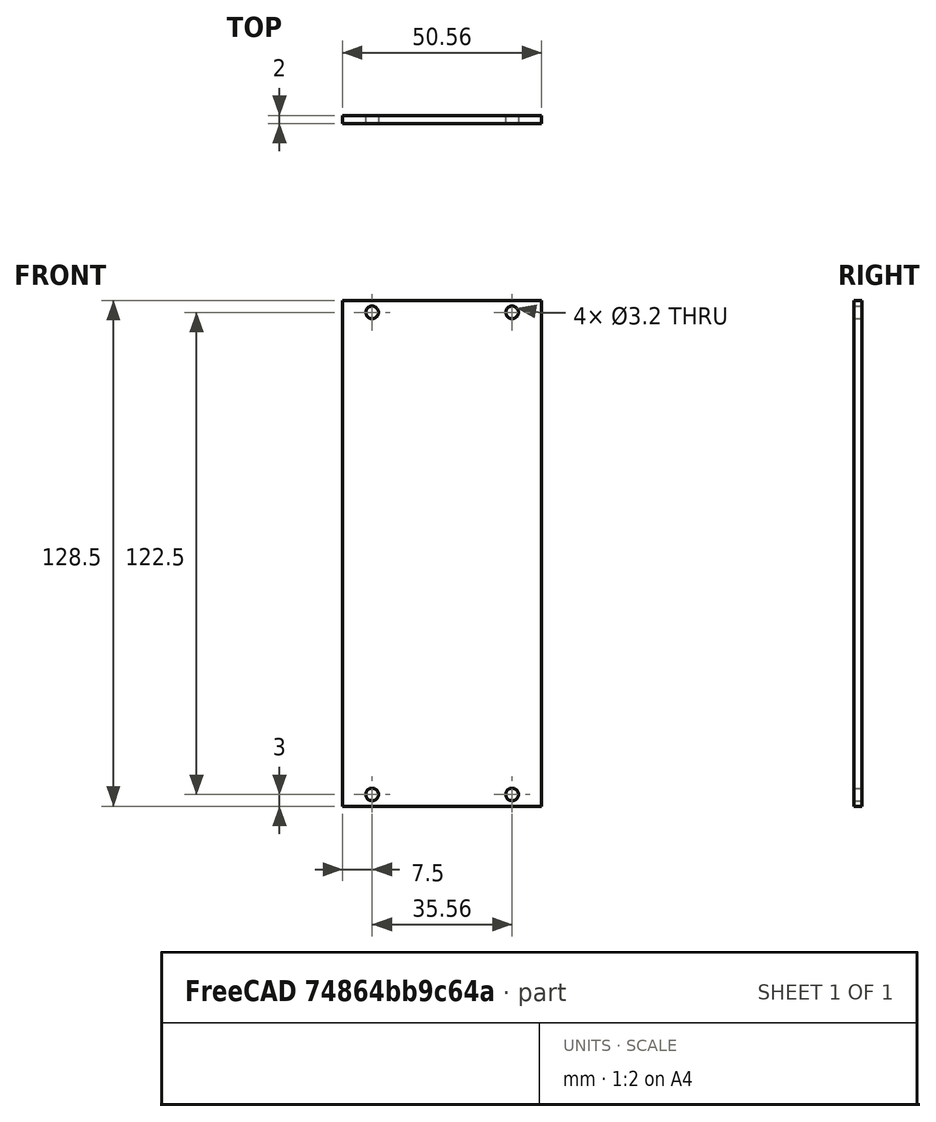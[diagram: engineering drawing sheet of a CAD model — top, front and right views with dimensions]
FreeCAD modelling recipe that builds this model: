
FCSTD DOCUMENT  (FreeCAD 1.0R38641 +468 (Git))
Label: 10hp_plate
License: All rights reserved
LicenseURL: https://en.wikipedia.org/wiki/All_rights_reserved
objects: Sketcher::SketchObject×1, PartDesign::Pad×1, PartDesign::Body×1, App::VarSet×1
note: 6 computed .brp shape members not serialized (recipe doc carries the construction recipe); baked Part::Feature solids carry a one-line shape summary decoded from their .brp
EXTERNAL_REF file=plate_dims.FCStd obj=VarSet

FEATURE [Sketcher::SketchObject] Sketch
  ArcFitTolerance = 1e-06
  AttachmentSupport = -> [XZ_Plane]
  FullyConstrained = true
  MakeInternals = false
  MapMode = 5
  Placement = pos=(0,0,0) rot=(1,0,0;1.5708rad)
  expr: Constraints[39] = <<plate_dims>>#VarSet.HoleOffsetY
  expr: Constraints[40] = <<plate_dims>>#VarSet.HoleOffsetX
  expr: Constraints[48] = <<plate_dims>>#VarSet.HoleDiameter
  expr: Constraints[49] = <<plate_dims>>#VarSet.PlateHeight
  expr: Constraints[52] = <<plate_dims>>#VarSet.HoleSpacing * (VarSet.PlateWidthHP - 3)
  sketch-geometry (20):
    g0: LineSegment StartX=-25.28 StartY=64.25 StartZ=0 EndX=-25.28 EndY=-64.25 EndZ=0
    g1: LineSegment StartX=-25.28 StartY=-64.25 StartZ=0 EndX=25.28 EndY=-64.25 EndZ=0
    g2: LineSegment StartX=25.28 StartY=-64.25 StartZ=0 EndX=25.28 EndY=64.25 EndZ=0
    g3: LineSegment StartX=25.28 StartY=64.25 StartZ=0 EndX=-25.28 EndY=64.25 EndZ=0
    g4: LineSegment [constr] StartX=17.78 StartY=61.25 StartZ=0 EndX=25.28 EndY=61.25 EndZ=0
    g5: LineSegment [constr] StartX=17.78 StartY=64.25 StartZ=0 EndX=17.78 EndY=61.25 EndZ=0
    g6: LineSegment [constr] StartX=17.78 StartY=61.25 StartZ=0 EndX=17.78 EndY=-61.25 EndZ=0
    g7: LineSegment [constr] StartX=17.78 StartY=-61.25 StartZ=0 EndX=17.78 EndY=-64.25 EndZ=0
    g8: LineSegment [constr] StartX=17.78 StartY=-61.25 StartZ=0 EndX=25.28 EndY=-61.25 EndZ=0
    g9: LineSegment [constr] StartX=-17.78 StartY=-61.25 StartZ=0 EndX=-17.78 EndY=-64.25 EndZ=0
    g10: LineSegment [constr] StartX=-25.28 StartY=-61.25 StartZ=0 EndX=-17.78 EndY=-61.25 EndZ=0
    g11: LineSegment [constr] StartX=-17.78 StartY=-61.25 StartZ=0 EndX=17.78 EndY=-61.25 EndZ=0
    g12: LineSegment [constr] StartX=-25.28 StartY=61.25 StartZ=0 EndX=-17.78 EndY=61.25 EndZ=0
    g13: LineSegment [constr] StartX=-17.78 StartY=61.25 StartZ=0 EndX=17.78 EndY=61.25 EndZ=0
    g14: LineSegment [constr] StartX=-17.78 StartY=64.25 StartZ=0 EndX=-17.78 EndY=61.25 EndZ=0
    g15: LineSegment [constr] StartX=-17.78 StartY=61.25 StartZ=0 EndX=-17.78 EndY=-61.25 EndZ=0
    g16: Circle CenterX=-17.78 CenterY=61.25 CenterZ=0 NormalX=0 NormalY=0 NormalZ=1 AngleXU=0 Radius=1.6
    g17: Circle CenterX=17.78 CenterY=61.25 CenterZ=0 NormalX=0 NormalY=0 NormalZ=1 AngleXU=0 Radius=1.6
    g18: Circle CenterX=17.78 CenterY=-61.25 CenterZ=0 NormalX=0 NormalY=0 NormalZ=1 AngleXU=0 Radius=1.6
    g19: Circle CenterX=-17.78 CenterY=-61.25 CenterZ=0 NormalX=0 NormalY=0 NormalZ=1 AngleXU=0 Radius=1.6
  constraints (58):
    c: Coincident(g0,g1)
    c: Coincident(g1,g2)
    c: Coincident(g2,g3)
    c: Coincident(g3,g0)
    c: Vertical(g2)
    c: Horizontal(g1)
    c: PointOnObject(g14,g3)
    c: PointOnObject(g9,g1)
    c: PointOnObject(g12,g0)
    c: PointOnObject(g4,g2)
    c: PointOnObject(g10,g0)
    c: PointOnObject(g8,g2)
    c: PointOnObject(g5,g3)
    c: PointOnObject(g7,g1)
    c: Coincident(g13,g4)
    c: Horizontal(g4)
    c: Coincident(g5,g6)
    c: Vertical(g5)
    c: Coincident(g6,g7)
    c: Vertical(g6)
    c: Vertical(g7)
    c: Coincident(g11,g8)
    c: Horizontal(g8)
    c: Coincident(g15,g9)
    c: Vertical(g9)
    c: Coincident(g10,g11)
    c: Horizontal(g10)
    c: Horizontal(g11)
    c: Coincident(g12,g13)
    c: Horizontal(g12)
    c: Horizontal(g13)
    c: Coincident(g14,g15)
    c: Vertical(g14)
    c: Vertical(g15)
    c: Coincident(g12,g14)
    c: Coincident(g9,g10)
    c: Coincident(g8,g6)
    c: Coincident(g4,g5)
    c: Equal(g9,g14)
    c: Distance(g9,g9) = 3
    c: Distance(g10,g10) = 7.5
    c: Coincident(g16,g12)
    c: Coincident(g17,g4)
    c: Coincident(g18,g6)
    c: Coincident(g19,g9)
    c: Equal(g19,g18)
    c: Equal(g18,g17)
    c: Equal(g17,g16)
    c: Diameter(g16) = 3.2
    c: DistanceY(g0,g0) = 128.5
    c: Distance(g12,g9) = 125.5
    c: Distance(g14,g14) = 3
    c: Distance(g11,g11) = 35.56
    c: Distance(g1,g1) = 50.56
    c: Symmetric(g0,g2,g-2)
    c: Symmetric(g0,g0,g-1)
    c: Distance(g8,g8) = 7.5
    c: Equal(g8,g10)
FEATURE [PartDesign::Pad] Pad
  Direction = (0,-1,2e-16)
  Length = 2
  Length2 = 10
  Placement = pos=(0,0,0) rot=(1,0,0;1.5708rad)
  Profile = -> Sketch
  ReferenceAxis = -> Sketch [N_Axis]
  Refine = true
  Suppressed = false
  Type = 0
FEATURE [PartDesign::Body] Body  label="10HpPlate"
  AllowCompound = false
  Group = -> [Sketch,Pad]
  Origin = -> Origin
  Tip = -> Pad
FEATURE [App::VarSet] VarSet
  PlateWidthHP = 10
